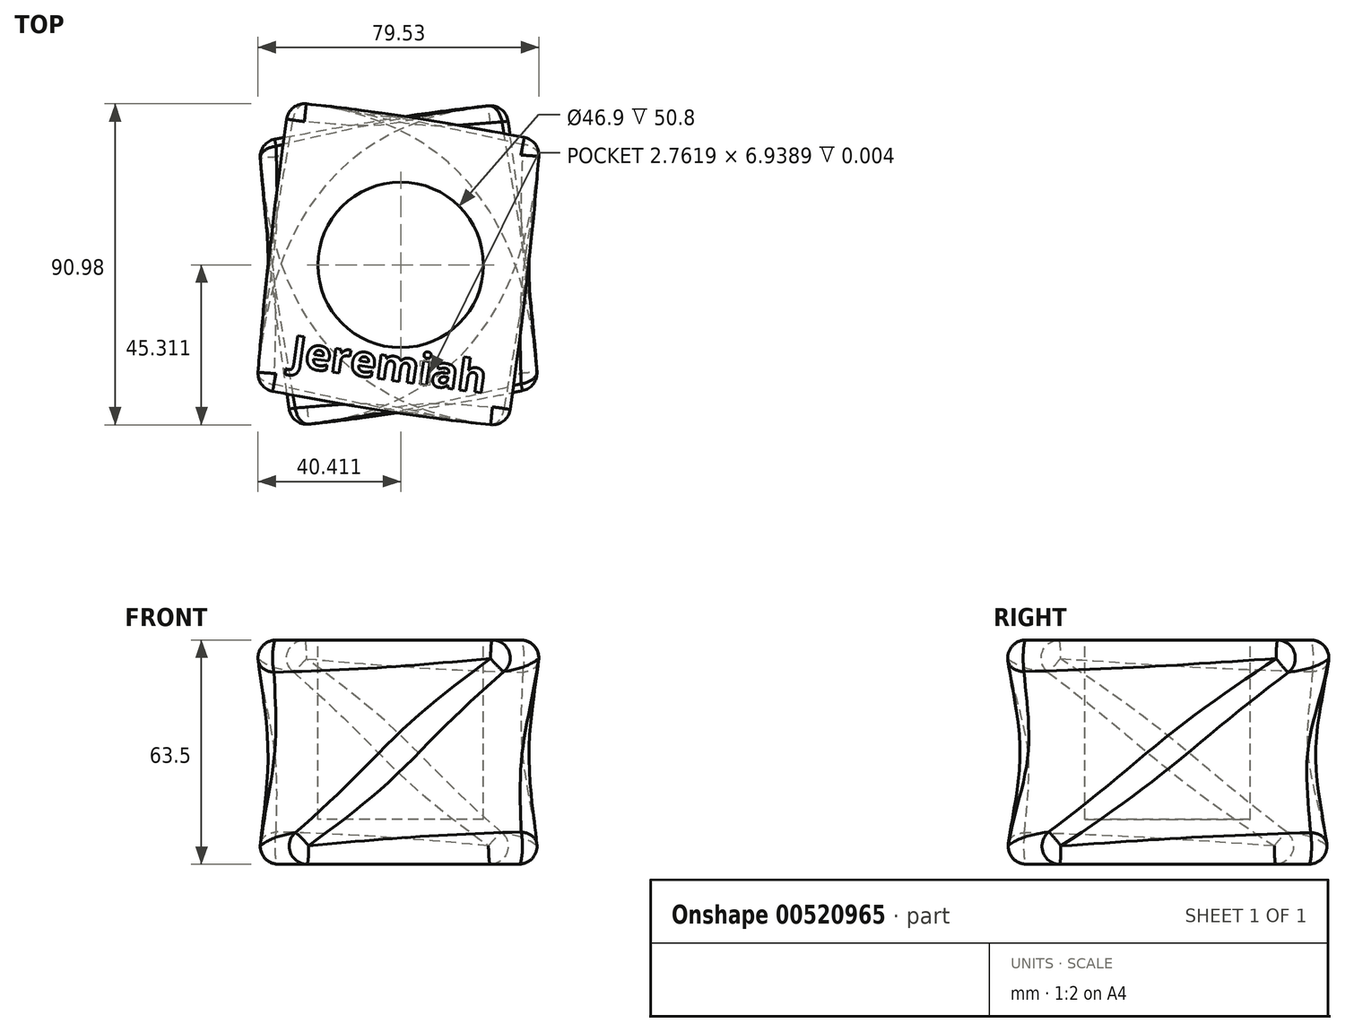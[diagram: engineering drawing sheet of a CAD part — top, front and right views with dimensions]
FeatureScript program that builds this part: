
annotation { "Feature Type Name" : "Feature", "Feature Type Description" : "" }
export const myFeature = defineFeature(function(context is Context, id is Id, definition is map)
    precondition{}
    {
        {
            var Q0;
            Q0=qCreatedBy(makeId("Top.planeOp"),FACE);
            var sketch = newSketch(context, id + "F0", { "sketchPlane" : qUnion([Q0])});
            skLineSegment(sketch, "E0.bottom", {"start": v(-43.06, 40.82) * mm, "end": v(36.48, 40.82) * mm});
            skLineSegment(sketch, "E0.top", {"start": v(-43.06, -50.96) * mm, "end": v(36.48, -50.96) * mm});
            skLineSegment(sketch, "E0.left", {"start": v(-43.06, 40.82) * mm, "end": v(-43.06, -50.96) * mm});
            skLineSegment(sketch, "E0.right", {"start": v(36.48, 40.82) * mm, "end": v(36.48, -50.96) * mm});
            skSolve(sketch);
        }
        {
            var Q0;
            Q0=qCreatedBy(makeId("Top.planeOp"),FACE);
            cPlane(context, id + "F1", {"entities" : qUnion([Q0]), "cplaneType" : CPlaneType.OFFSET, "offset" : 63.5 * mm, "width" : 152.4 * mm, "height" : 152.4 * mm});
        }
        {
            var Q0;
            Q0=qCreatedBy(id+"F1.planeOp",FACE);
            var sketch = newSketch(context, id + "F2", { "sketchPlane" : qUnion([Q0])});
            skLineSegment(sketch, "E1.bottom", {"start": v(-43.8, 41.47) * mm, "end": v(37.08, 41.47) * mm});
            skLineSegment(sketch, "E1.top", {"start": v(-43.8, -51.1) * mm, "end": v(37.08, -51.1) * mm});
            skLineSegment(sketch, "E1.left", {"start": v(-43.8, 41.47) * mm, "end": v(-43.8, -51.1) * mm});
            skLineSegment(sketch, "E1.right", {"start": v(37.08, 41.47) * mm, "end": v(37.08, -51.1) * mm});
            skSolve(sketch);
        }
        {
            var Q0;
            Q0=makeQuery(id+"F0.imprint","IMPRINT",FACE,{"disambiguationData":[TD([[makeQuery(id+"F0.imprint","IMPRINT",EDGE,{"derivedFrom":sQuery(id+"F0.wireOp",EDGE,"E0.bottom")}),-1.0]])]});
            var Q1;
            Q1=makeQuery(id+"F2.imprint","IMPRINT",FACE,{"disambiguationData":[TD([[makeQuery(id+"F2.imprint","IMPRINT",EDGE,{"derivedFrom":sQuery(id+"F2.wireOp",EDGE,"E1.bottom")}),-1.0]])]});
            var Q2;
            Q2=sQuery(id+"F2.wireOp",VERTEX,"E1.top.start");
            var Q3;
            Q3=sQuery(id+"F0.wireOp",VERTEX,"E0.bottom.start");
            loft(context, id + "F3", {"sheetProfilesArray" : [{ "sheetProfileEntities" : qUnion([Q0]) }, { "sheetProfileEntities" : qUnion([Q1]) }], "matchConnections" : true, "connections" : [{ "connectionEntities" : qUnion([Q2, Q3]), "connectionEdgeQueries" : qUnion([]), "connectionEdgeParameters" : [] }]});
        }
        {
            var Q0;
            Q0=makeQuery(id+"F3.opLoft","SWEPT_EDGE",EDGE,{"disambiguationData":[OSD([sQuery(id+"F0.wireOp",EDGE,"E0.bottom"),sQuery(id+"F0.wireOp",EDGE,"E0.left"),sQuery(id+"F2.wireOp",EDGE,"E1.top"),sQuery(id+"F2.wireOp",EDGE,"E1.left")])]});
            var Q1;
            Q1=makeQuery(id+"F3.opLoft","SWEPT_EDGE",EDGE,{"disambiguationData":[OSD([sQuery(id+"F0.wireOp",EDGE,"E0.bottom"),sQuery(id+"F0.wireOp",EDGE,"E0.right"),sQuery(id+"F2.wireOp",EDGE,"E1.bottom"),sQuery(id+"F2.wireOp",EDGE,"E1.left")])]});
            var Q2;
            Q2=makeQuery(id+"F3.opLoft","MID_CAP_EDGE",EDGE,{"disambiguationData":[OSD([sQuery(id+"F0.wireOp",EDGE,"E0.bottom"),sQuery(id+"F0.wireOp",EDGE,"E0.left"),sQuery(id+"F0.wireOp",EDGE,"E0.right")])],"capPos":0.0});
            var Q3;
            Q3=makeQuery(id+"F3.opLoft","MID_CAP_EDGE",EDGE,{"disambiguationData":[OSD([sQuery(id+"F2.wireOp",EDGE,"E1.bottom"),sQuery(id+"F2.wireOp",EDGE,"E1.top"),sQuery(id+"F2.wireOp",EDGE,"E1.left")])],"capPos":1.0});
            var Q4;
            Q4=makeQuery(id+"F3.opLoft","MID_CAP_EDGE",EDGE,{"disambiguationData":[OSD([sQuery(id+"F0.wireOp",EDGE,"E0.bottom"),sQuery(id+"F0.wireOp",EDGE,"E0.top"),sQuery(id+"F0.wireOp",EDGE,"E0.left")])],"capPos":0.0});
            var Q5;
            Q5=makeQuery(id+"F3.opLoft","MID_CAP_EDGE",EDGE,{"disambiguationData":[OSD([sQuery(id+"F0.wireOp",EDGE,"E0.bottom"),sQuery(id+"F0.wireOp",EDGE,"E0.top"),sQuery(id+"F0.wireOp",EDGE,"E0.left")])],"capPos":0.0});
            var Q6;
            Q6=makeQuery(id+"F3.opLoft","SWEPT_EDGE",EDGE,{"disambiguationData":[OSD([sQuery(id+"F0.wireOp",EDGE,"E0.top"),sQuery(id+"F0.wireOp",EDGE,"E0.right"),sQuery(id+"F2.wireOp",EDGE,"E1.bottom"),sQuery(id+"F2.wireOp",EDGE,"E1.right")])]});
            var Q7;
            Q7=makeQuery(id+"F3.opLoft","MID_CAP_EDGE",EDGE,{"disambiguationData":[OSD([sQuery(id+"F2.wireOp",EDGE,"E1.bottom"),sQuery(id+"F2.wireOp",EDGE,"E1.left"),sQuery(id+"F2.wireOp",EDGE,"E1.right")])],"capPos":1.0});
            var Q8;
            Q8=makeQuery(id+"F3.opLoft","MID_CAP_EDGE",EDGE,{"disambiguationData":[OSD([sQuery(id+"F2.wireOp",EDGE,"E1.top"),sQuery(id+"F2.wireOp",EDGE,"E1.left"),sQuery(id+"F2.wireOp",EDGE,"E1.right")])],"capPos":1.0});
            var Q9;
            Q9=makeQuery(id+"F3.opLoft","MID_CAP_EDGE",EDGE,{"disambiguationData":[OSD([sQuery(id+"F2.wireOp",EDGE,"E1.bottom"),sQuery(id+"F2.wireOp",EDGE,"E1.top"),sQuery(id+"F2.wireOp",EDGE,"E1.right")])],"capPos":1.0});
            var Q10;
            Q10=makeQuery(id+"F3.opLoft","SWEPT_EDGE",EDGE,{"disambiguationData":[OSD([sQuery(id+"F0.wireOp",EDGE,"E0.top"),sQuery(id+"F0.wireOp",EDGE,"E0.left"),sQuery(id+"F2.wireOp",EDGE,"E1.top"),sQuery(id+"F2.wireOp",EDGE,"E1.right")])]});
            var Q11;
            Q11=makeQuery(id+"F3.opLoft","MID_CAP_EDGE",EDGE,{"disambiguationData":[OSD([sQuery(id+"F0.wireOp",EDGE,"E0.top"),sQuery(id+"F0.wireOp",EDGE,"E0.left"),sQuery(id+"F0.wireOp",EDGE,"E0.right")])],"capPos":0.0});
            var Q12;
            Q12=makeQuery(id+"F3.opLoft","MID_CAP_EDGE",EDGE,{"disambiguationData":[OSD([sQuery(id+"F0.wireOp",EDGE,"E0.bottom"),sQuery(id+"F0.wireOp",EDGE,"E0.top"),sQuery(id+"F0.wireOp",EDGE,"E0.right")])],"capPos":0.0});
            fillet(context, id + "F4", {"entities" : qUnion([Q0, Q1, Q2, Q3, Q4, Q5, Q6, Q7, Q8, Q9, Q10, Q11, Q12]), "radius" : 5.08 * mm, "tangentPropagation" : true, "allowEdgeOverflow" : false});
        }
        {
            var Q0;
            Q0=makeQuery(id+"F3.opLoft","CAP_FACE",FACE,{"disambiguationData":[OSD([makeQuery(id+"F2.imprint","IMPRINT",FACE,{"disambiguationData":[TD([[makeQuery(id+"F2.imprint","IMPRINT",EDGE,{"derivedFrom":sQuery(id+"F2.wireOp",EDGE,"E1.bottom")}),-1.0]])]})])],"isStart":true});
            var sketch = newSketch(context, id + "F5", { "sketchPlane" : qUnion([Q0])});
            skCircle(sketch, "E2", {"center": v(-2.7, -5.02) * mm, "radius": 23.45 * mm});
            skSolve(sketch);
        }
        {
            var Q0;
            Q0=makeQuery(id+"F5.imprint","IMPRINT",FACE,{"disambiguationData":[TD([[makeQuery(id+"F5.imprint","IMPRINT",EDGE,{"derivedFrom":sQuery(id+"F5.wireOp",EDGE,"E2")}),1.0]])]});
            extrude(context, id + "F6", {"entities" : qUnion([Q0]), "operationType" : NewBodyOperationType.REMOVE, "oppositeDirection" : true, "depth" : 50.8 * mm, "offsetDistance" : 25.4 * mm});
        }
        {
            var Q0;
            Q0=makeQuery(id+"F3.opLoft","CAP_FACE",FACE,{"disambiguationData":[OSD([makeQuery(id+"F2.imprint","IMPRINT",FACE,{"disambiguationData":[TD([[makeQuery(id+"F2.imprint","IMPRINT",EDGE,{"derivedFrom":sQuery(id+"F2.wireOp",EDGE,"E1.bottom")}),-1.0]])]})])],"isStart":true});
            var sketch = newSketch(context, id + "F7", { "sketchPlane" : qUnion([Q0])});
            skText(sketch, "E3", { "text": "Jeremiah", "fontName": "OpenSans-Bold.ttf"});
            const initialGuessF7  = {"E3": [-0.03423, -0.03366, 0.99027, -0.13917, 0.0089]};
            skSetInitialGuess(sketch, initialGuessF7);
            skSolve(sketch);
        }
        {
            var Q0;
            Q0 = qSketchRegion(id + "F7", true);
            extrude(context, id + "F8", {"entities" : qUnion([Q0]), "operationType" : NewBodyOperationType.REMOVE, "oppositeDirection" : true, "depth" : 1 / 254 * mm, "offsetDistance" : 25.4 * mm});
        }
    });
